FCSTD DOCUMENT  (FreeCAD 1.0R38806 (Git))
Label: Unnamed
License: All rights reserved
LicenseURL: https://en.wikipedia.org/wiki/All_rights_reserved
objects: Sketcher::SketchObject×1
note: 2 computed .brp shape members not serialized (recipe doc carries the construction recipe); baked Part::Feature solids carry a one-line shape summary decoded from their .brp

FEATURE [Sketcher::SketchObject] Sketch
  ArcFitTolerance = 1e-06
  FullyConstrained = false
  MakeInternals = false
  sketch-geometry (10):
    g0: LineSegment StartX=0 StartY=0 StartZ=0 EndX=6 EndY=0 EndZ=0
    g1: LineSegment StartX=0 StartY=0 StartZ=0 EndX=-3.38169 EndY=2.1364 EndZ=0
    g2: LineSegment StartX=6 StartY=0 StartZ=0 EndX=9.38169 EndY=2.1364 EndZ=0
    g3: LineSegment StartX=-3.38169 StartY=2.1364 StartZ=0 EndX=0.655064 EndY=6.57539 EndZ=0
    g4: LineSegment StartX=9.38169 StartY=2.1364 StartZ=0 EndX=5.34494 EndY=6.57539 EndZ=0
    g5: LineSegment StartX=1.06931 StartY=7.74778 StartZ=0 EndX=1.06931 EndY=3.74778 EndZ=0
    g6: LineSegment StartX=1.06931 StartY=3.74778 StartZ=0 EndX=5.06931 EndY=3.74778 EndZ=0
    g7: LineSegment StartX=5.06931 StartY=3.74778 StartZ=0 EndX=5.06931 EndY=7.74778 EndZ=0
    g8: LineSegment StartX=5.06931 StartY=7.74778 StartZ=0 EndX=1.06931 EndY=7.74778 EndZ=0
    g9: LineSegment StartX=3 StartY=-1.14513 StartZ=0 EndX=3 EndY=-4.88974 EndZ=0
  constraints (25):
    c: DistanceX(g0,g0) = 6
    c: Coincident(g0,g-1)
    c: Distance(g1) = 4
    c: Coincident(g1,g0)
    c: Coincident(g2,g0)
    c: PointOnObject(g0,g-1)
    c: Coincident(g3,g1)
    c: Coincident(g4,g2)
    c: Angle(g1,g3) = 1.39626
    c: Angle(g4,g2) = 1.39626
    c: Distance(g3,g3) = 6
    c: Distance(g4,g4) = 6
    c: Distance(g2,g2) = 4
    c: Coincident(g5,g6)
    c: Coincident(g6,g7)
    c: Coincident(g7,g8)
    c: Coincident(g8,g5)
    c: Vertical(g5)
    c: Vertical(g7)
    c: Horizontal(g6)
    c: Horizontal(g8)
    c: Distance(g5,g7) = 4
    c: Distance(g6,g8) = 4
    c: Vertical(g9)
    c: Symmetric(g3,g4,g9)
